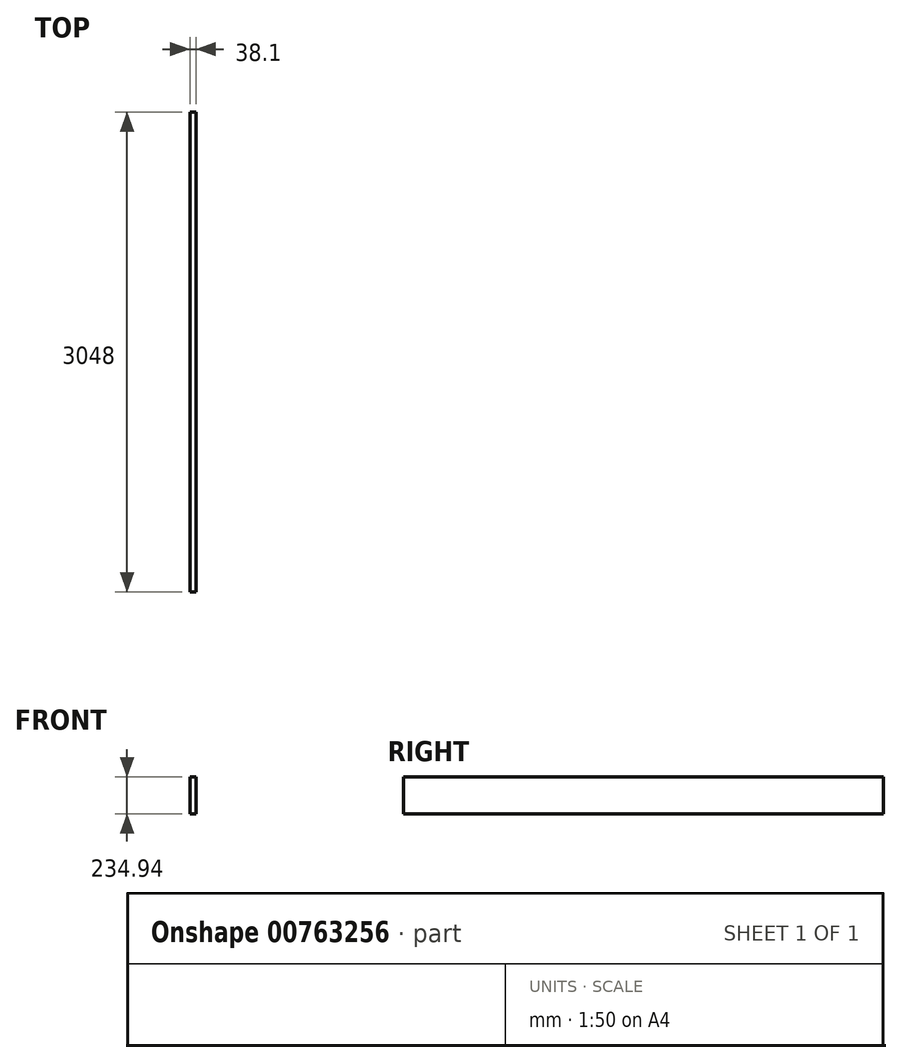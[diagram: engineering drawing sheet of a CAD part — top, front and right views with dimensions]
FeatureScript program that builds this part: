
annotation { "Feature Type Name" : "Feature", "Feature Type Description" : "" }
export const myFeature = defineFeature(function(context is Context, id is Id, definition is map)
    precondition{}
    {
        {
            var Q0;
            Q0=qCreatedBy(makeId("Front.planeOp"),FACE);
            var sketch = newSketch(context, id + "F0", { "sketchPlane" : qUnion([Q0])});
            skLineSegment(sketch, "E0.bottom", {"start": v(19.05, 117.48) * mm, "end": v(-19.05, 117.48) * mm});
            skLineSegment(sketch, "E0.top", {"start": v(19.05, -117.48) * mm, "end": v(-19.05, -117.48) * mm});
            skLineSegment(sketch, "E0.left", {"start": v(19.05, 117.48) * mm, "end": v(19.05, -117.48) * mm});
            skLineSegment(sketch, "E0.right", {"start": v(-19.05, 117.48) * mm, "end": v(-19.05, -117.48) * mm});
            skPoint(sketch, "E0.middle", {"position": v(0, 0) * mm});
            skSolve(sketch);
        }
        {
            var Q0;
            Q0 = qSketchRegion(id + "F0", true);
            extrude(context, id + "F1", {"entities" : qUnion([Q0]), "depth" : 3048 * mm, "offsetDistance" : 25.4 * mm});
        }
    });
